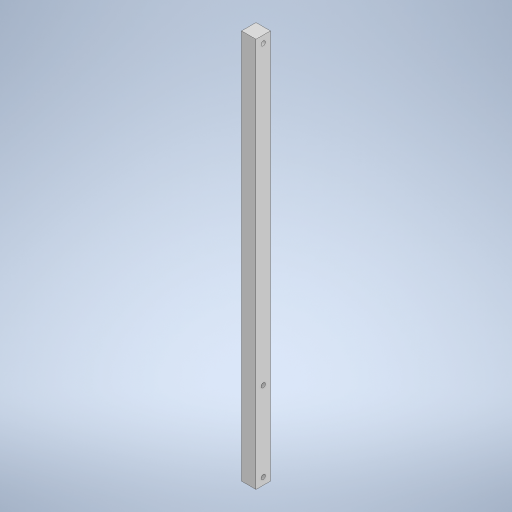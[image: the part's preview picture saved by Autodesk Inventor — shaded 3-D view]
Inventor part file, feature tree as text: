
AUTODESK INVENTOR PART (.ipt)
format: ipt  version: 2023 (Build 270158000, 158)  size: 243,712 bytes
history: native  units: mm
features: sketch x2, other x1, extrude x1, hole x1
ambient origin geometry x8: Origin, YZ Plane, XZ Plane, XY Plane, X Axis, Y Axis, Z Axis, Center Point
bodies: Body1 (feature_tree)
feature tree (5):
  other  "ソリッド1"
  extrude  "押し出し1"  Depth=270.0mm
  hole  "穴1"  [1 undecoded]
  sketch  "スケッチ1"
  sketch  "スケッチ2"
note: 1 required parameter value undecoded (feature->parameter linkage not recoverable at this tier; creation-order binding heuristic only, values carry confidence <= 0.55)
